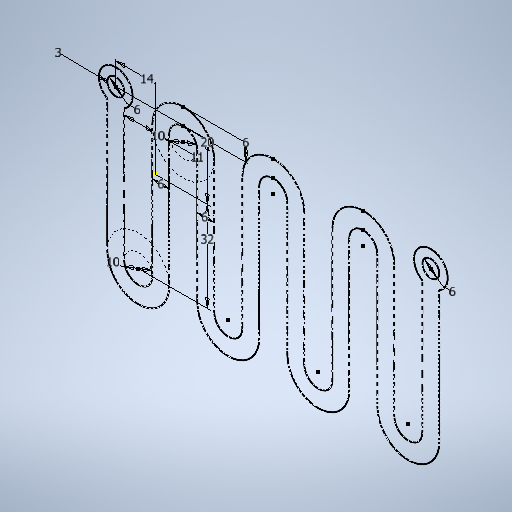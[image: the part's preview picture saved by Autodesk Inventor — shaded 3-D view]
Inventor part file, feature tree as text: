
AUTODESK INVENTOR PART (.ipt)
format: ipt  version: 2025.2 (Build 292293000, 293)  size: 291,840 bytes
history: native  units: mm
features: sketch x1
ambient origin geometry x8: Origin, YZ Plane, XZ Plane, XY Plane, X Axis, Y Axis, Z Axis, Center Point
feature tree (1):
  sketch  "Sketch1"  dims[d1=20.0mm d2=14.0mm d7=11.0mm d8=6.0mm d9=3.0mm d16=10.0mm d20=32.0mm d25=6.0mm d29=10.0mm d36=6.0mm d39=6.0mm d41=6.0mm]
